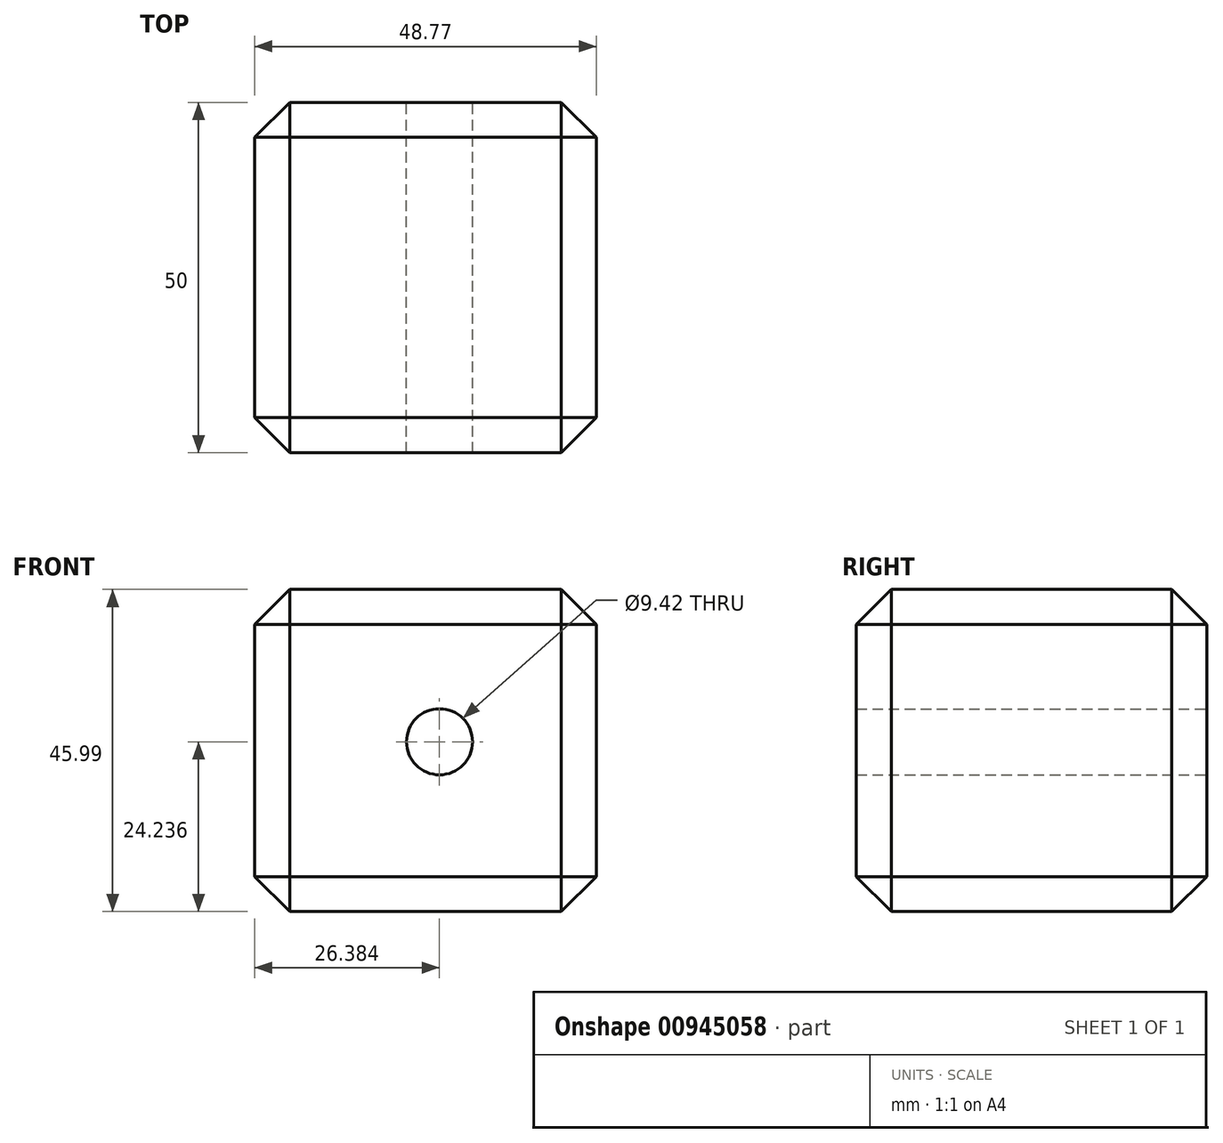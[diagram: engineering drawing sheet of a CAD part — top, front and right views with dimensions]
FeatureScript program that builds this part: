
annotation { "Feature Type Name" : "Feature", "Feature Type Description" : "" }
export const myFeature = defineFeature(function(context is Context, id is Id, definition is map)
    precondition{}
    {
        {
            var Q0;
            Q0=qCreatedBy(makeId("Front.planeOp"),FACE);
            var sketch = newSketch(context, id + "F0", { "sketchPlane" : qUnion([Q0])});
            skLineSegment(sketch, "E0.bottom", {"start": v(0, 0) * mm, "end": v(48.77, 0) * mm});
            skLineSegment(sketch, "E0.top", {"start": v(0, 45.99) * mm, "end": v(48.77, 45.99) * mm});
            skLineSegment(sketch, "E0.left", {"start": v(0, 0) * mm, "end": v(0, 45.99) * mm});
            skLineSegment(sketch, "E0.right", {"start": v(48.77, 0) * mm, "end": v(48.77, 45.99) * mm});
            skSolve(sketch);
        }
        {
            var Q0;
            Q0 = qSketchRegion(id + "F0", true);
            extrude(context, id + "F1", {"entities" : qUnion([Q0]), "depth" : 50 * mm, "offsetDistance" : 25 * mm});
        }
        {
            var Q0;
            Q0=makeQuery(id+"F1.opExtrude","CAP_FACE",FACE,{"disambiguationData":[OSD([sQuery(id+"F0.wireOp",EDGE,"E0.bottom"),sQuery(id+"F0.wireOp",EDGE,"E0.top"),sQuery(id+"F0.wireOp",EDGE,"E0.left"),sQuery(id+"F0.wireOp",EDGE,"E0.right")])],"isStart":false});
            var Q1;
            Q1=makeQuery(id+"F1.opExtrude","SWEPT_FACE",FACE,{"disambiguationData":[OSD([sQuery(id+"F0.wireOp",EDGE,"E0.right")])]});
            var Q2;
            Q2=makeQuery(id+"F1.opExtrude","SWEPT_FACE",FACE,{"disambiguationData":[OSD([sQuery(id+"F0.wireOp",EDGE,"E0.top")])]});
            var Q3;
            Q3=makeQuery(id+"F1.opExtrude","SWEPT_FACE",FACE,{"disambiguationData":[OSD([sQuery(id+"F0.wireOp",EDGE,"E0.bottom")])]});
            var Q4;
            Q4=makeQuery(id+"F1.opExtrude","CAP_FACE",FACE,{"disambiguationData":[OSD([sQuery(id+"F0.wireOp",EDGE,"E0.bottom"),sQuery(id+"F0.wireOp",EDGE,"E0.top"),sQuery(id+"F0.wireOp",EDGE,"E0.left"),sQuery(id+"F0.wireOp",EDGE,"E0.right")])],"isStart":true});
            chamfer(context, id + "F2", {"entities" : qUnion([Q0, Q1, Q2, Q3, Q4]), "width" : 5 * mm, "tangentPropagation" : true});
        }
        {
            var Q0;
            Q0=makeQuery(id+"F1.opExtrude","CAP_FACE",FACE,{"disambiguationData":[OSD([sQuery(id+"F0.wireOp",EDGE,"E0.bottom"),sQuery(id+"F0.wireOp",EDGE,"E0.top"),sQuery(id+"F0.wireOp",EDGE,"E0.left"),sQuery(id+"F0.wireOp",EDGE,"E0.right")])],"isStart":true});
            var sketch = newSketch(context, id + "F3", { "sketchPlane" : qUnion([Q0])});
            skCircle(sketch, "E1", {"center": v(-26.38, 24.24) * mm, "radius": 4.71 * mm});
            skSolve(sketch);
        }
        {
            var Q0;
            Q0 = qSketchRegion(id + "F3", true);
            extrude(context, id + "F4", {"entities" : qUnion([Q0]), "operationType" : NewBodyOperationType.REMOVE, "endBound" : BoundingType.THROUGH_ALL, "oppositeDirection" : true, "depth" : 25 * mm, "offsetDistance" : 25 * mm});
        }
    });
